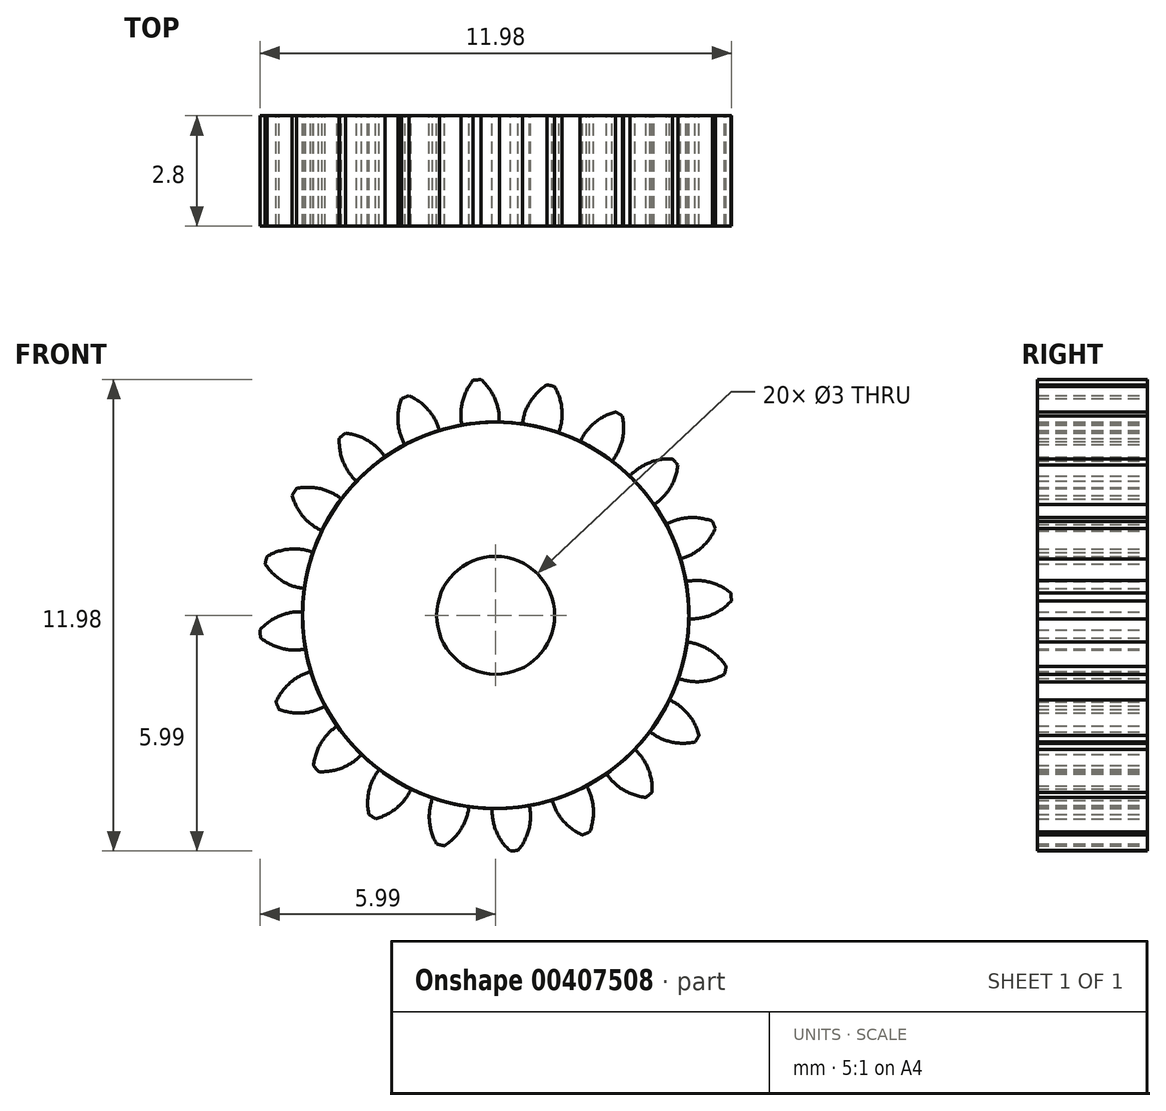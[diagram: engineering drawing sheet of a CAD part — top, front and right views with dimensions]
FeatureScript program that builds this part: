
annotation { "Feature Type Name" : "Feature", "Feature Type Description" : "" }
export const myFeature = defineFeature(function(context is Context, id is Id, definition is map)
    precondition{}
    {
        {
            var Q0;
            Q0=qCreatedBy(makeId("Front.planeOp"),FACE);
            var sketch = newSketch(context, id + "F0", { "sketchPlane" : qUnion([Q0])});
            skCircle(sketch, "E0", {"center": v(0, 0) * mm, "radius": 4.9 * mm});
            skCircle(sketch, "E1", {"center": v(0, 0) * mm, "radius": 5.46 * mm, "construction": true});
            skCircle(sketch, "E2", {"center": v(0, 0) * mm, "radius": 6 * mm, "construction": true});
            skLineSegment(sketch, "E3", {"start": v(0, 0) * mm, "end": v(0, 7.95) * mm, "construction": true});
            skLineSegment(sketch, "E4", {"start": v(0, 0) * mm, "end": v(-0.63, 8.03) * mm, "construction": true});
            skLineSegment(sketch, "E5", {"start": v(0, 5.46) * mm, "end": v(-5.48, 5.46) * mm, "construction": true});
            skLineSegment(sketch, "E6", {"start": v(0, 5.46) * mm, "end": v(-5.44, 3.47) * mm, "construction": true});
            skCircle(sketch, "E7", {"center": v(0, 0) * mm, "radius": 5.13 * mm, "construction": true});
            skCircle(sketch, "E8", {"center": v(0, 5.46) * mm, "radius": 1.37 * mm, "construction": true});
            skCircle(sketch, "E9", {"center": v(-1.27, 4.97) * mm, "radius": 1.37 * mm, "construction": true});
            skArc(sketch, "E10", {"start": v(0, 5.46) * mm, "mid": v(-0.15, 5.74) * mm, "end": v(-0.37, 5.99) * mm});
            skArc(sketch, "E11", {"start": v(0.09, 4.9) * mm, "mid": v(0.07, 5.19) * mm, "end": v(0, 5.46) * mm});
            skArc(sketch, "E12.MirrorCS", {"start": v(-0.85, 5.39) * mm, "mid": v(-0.75, 5.7) * mm, "end": v(-0.57, 5.97) * mm});
            skArc(sketch, "E13.MirrorCS", {"start": v(-0.86, 4.83) * mm, "mid": v(-0.88, 5.11) * mm, "end": v(-0.85, 5.39) * mm});
            skArc(sketch, "E14", {"start": v(-0.37, 5.99) * mm, "mid": v(-0.47, 5.98) * mm, "end": v(-0.57, 5.97) * mm});
            skSolve(sketch);
        }
        {
            var Q0;
            Q0=makeQuery(id+"F0.imprint","IMPRINT",FACE,{"disambiguationData":[TD([[makeQuery(id+"F0.imprint","IMPRINT",EDGE,{"derivedFrom":sQuery(id+"F0.wireOp",EDGE,"E10")}),1.0]])]});
            var Q1;
            {var subQ0=sQuery(id+"F0.wireOp",EDGE,"E0");var subQ1=makeQuery(id+"F0.imprint","INTERSECT",VERTEX,{"derivedFrom":[subQ0,sQuery(id+"F0.wireOp",EDGE,"E11")]});Q1=makeQuery(id+"F0.imprint","IMPRINT",FACE,{"disambiguationData":[TD([[makeQuery(id+"F0.imprint","IMPRINT",EDGE,{"disambiguationData":[TD([[subQ1,-1.0]])],"derivedFrom":subQ0}),1.0]])]});}
            extrude(context, id + "F1", {"entities" : qUnion([Q0, Q1]), "depth" : 2.8 * mm});
        }
        {
            var Q0;
            Q0=makeQuery(id+"F1.opExtrude","SWEPT_BODY",BODY,{"disambiguationData":[OSD([sQuery(id+"F0.wireOp",EDGE,"E0"),sQuery(id+"F0.wireOp",EDGE,"E10"),sQuery(id+"F0.wireOp",EDGE,"E11"),sQuery(id+"F0.wireOp",EDGE,"E12.MirrorCS"),sQuery(id+"F0.wireOp",EDGE,"E13.MirrorCS"),sQuery(id+"F0.wireOp",EDGE,"E14")])]});
            var Q1;
            Q1=makeQuery(id+"F1.opExtrude","SWEPT_FACE",FACE,{"disambiguationData":[OSD([sQuery(id+"F0.wireOp",EDGE,"E0")])]});
            circularPattern(context, id + "F2", {"entities" : qUnion([Q0]), "axis" : qUnion([Q1]), "angle" : 18 * degree, "instanceCount" : 20});
        }
        {
            var Q0;
            {var subQ0=sQuery(id+"F0.wireOp",EDGE,"E0");var subQ1=makeQuery(id+"F0.imprint","INTERSECT",VERTEX,{"derivedFrom":[subQ0,sQuery(id+"F0.wireOp",EDGE,"E11")]});Q0=makeQuery(id+"F0.imprint","IMPRINT",FACE,{"disambiguationData":[TD([[makeQuery(id+"F0.imprint","IMPRINT",EDGE,{"disambiguationData":[TD([[subQ1,-1.0]])],"derivedFrom":subQ0}),1.0]])]});}
            var sketch = newSketch(context, id + "F3", { "sketchPlane" : qUnion([Q0])});
            skCircle(sketch, "E15", {"center": v(0, 0) * mm, "radius": 1.5 * mm});
            skSolve(sketch);
        }
        {
            var Q0;
            Q0 = qSketchRegion(id + "F3", true);
            extrude(context, id + "F4", {"entities" : qUnion([Q0]), "operationType" : NewBodyOperationType.REMOVE, "depth" : 2.8 * mm});
        }
    });
